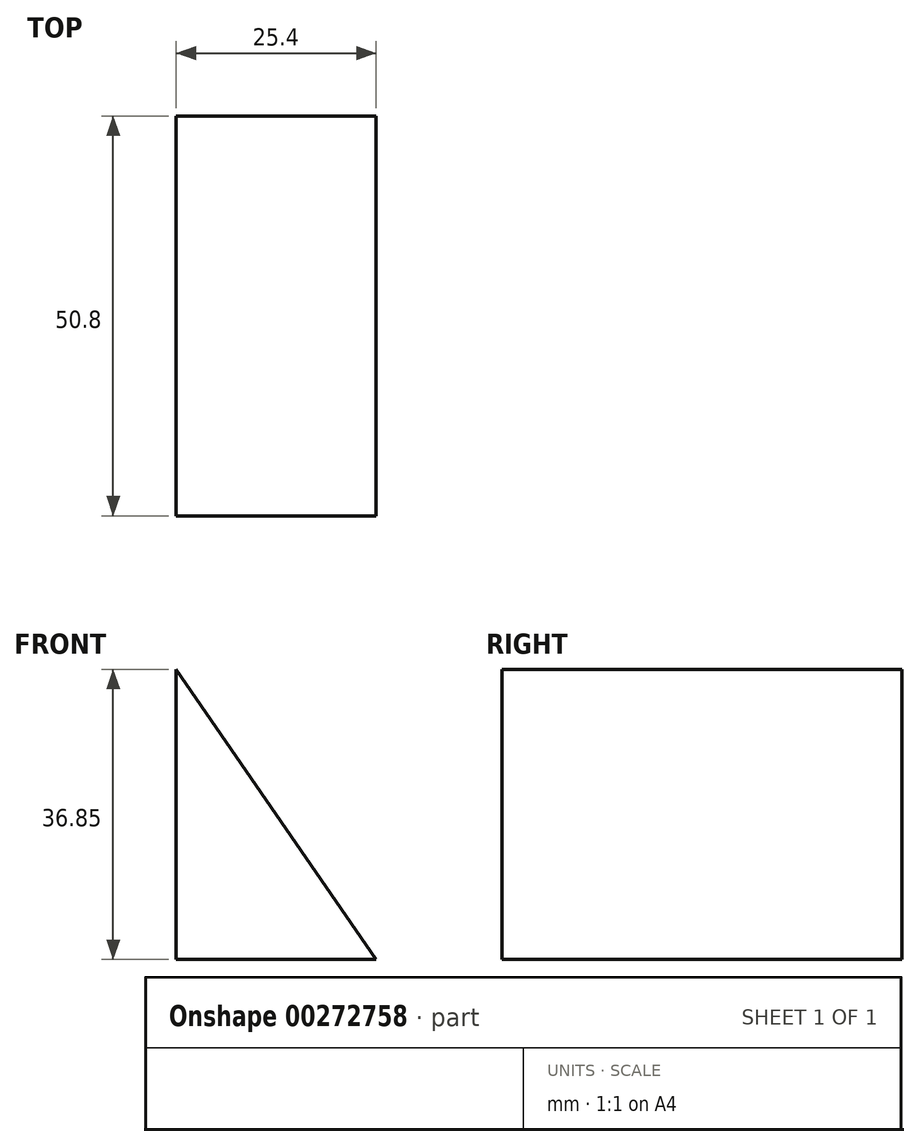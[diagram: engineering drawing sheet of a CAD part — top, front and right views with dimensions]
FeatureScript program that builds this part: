
annotation { "Feature Type Name" : "Feature", "Feature Type Description" : "" }
export const myFeature = defineFeature(function(context is Context, id is Id, definition is map)
    precondition{}
    {
        {
            var Q0;
            Q0=qCreatedBy(makeId("Front.planeOp"),FACE);
            var sketch = newSketch(context, id + "F0", { "sketchPlane" : qUnion([Q0])});
            skLineSegment(sketch, "E0", {"start": v(-63.2, 36.85) * mm, "end": v(-63.2, 0) * mm});
            skLineSegment(sketch, "E1", {"start": v(-63.2, 36.85) * mm, "end": v(-37.8, 0) * mm});
            skLineSegment(sketch, "E2", {"start": v(-63.2, 0) * mm, "end": v(-37.8, 0) * mm});
            skSolve(sketch);
        }
        {
            var Q0;
            Q0 = qSketchRegion(id + "F0", true);
            extrude(context, id + "F1", {"entities" : qUnion([Q0]), "depth" : 50.8 * mm});
        }
    });
